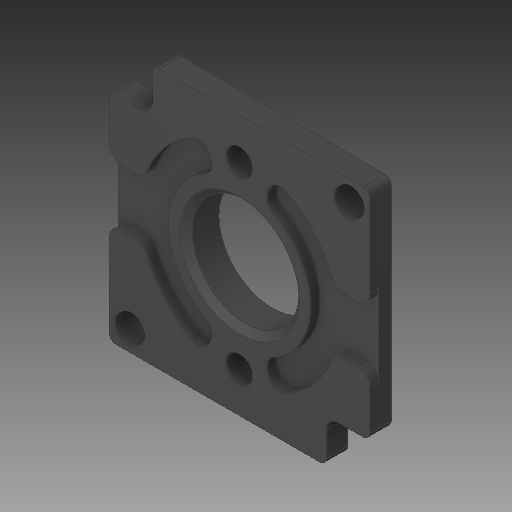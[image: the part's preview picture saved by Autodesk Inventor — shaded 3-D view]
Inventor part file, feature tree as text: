
AUTODESK INVENTOR PART (.ipt)
format: ipt  version: 2018 (Build 220112000, 112)  size: 272,384 bytes
history: native  units: in
note: dims shown in document units (in); Inventor stores cm internally (conversion verified against a paired STEP export)
features: fillet x1
ambient origin geometry x8: Origin, YZ Plane, XZ Plane, XY Plane, X Axis, Y Axis, Z Axis, Center Point
bodies: Solid1 (feature_tree)
feature tree (1):
  fillet  "Fillet4"  [1 undecoded]
note: 1 required parameter value undecoded (feature->parameter linkage not recoverable at this tier; creation-order binding heuristic only, values carry confidence <= 0.55)
